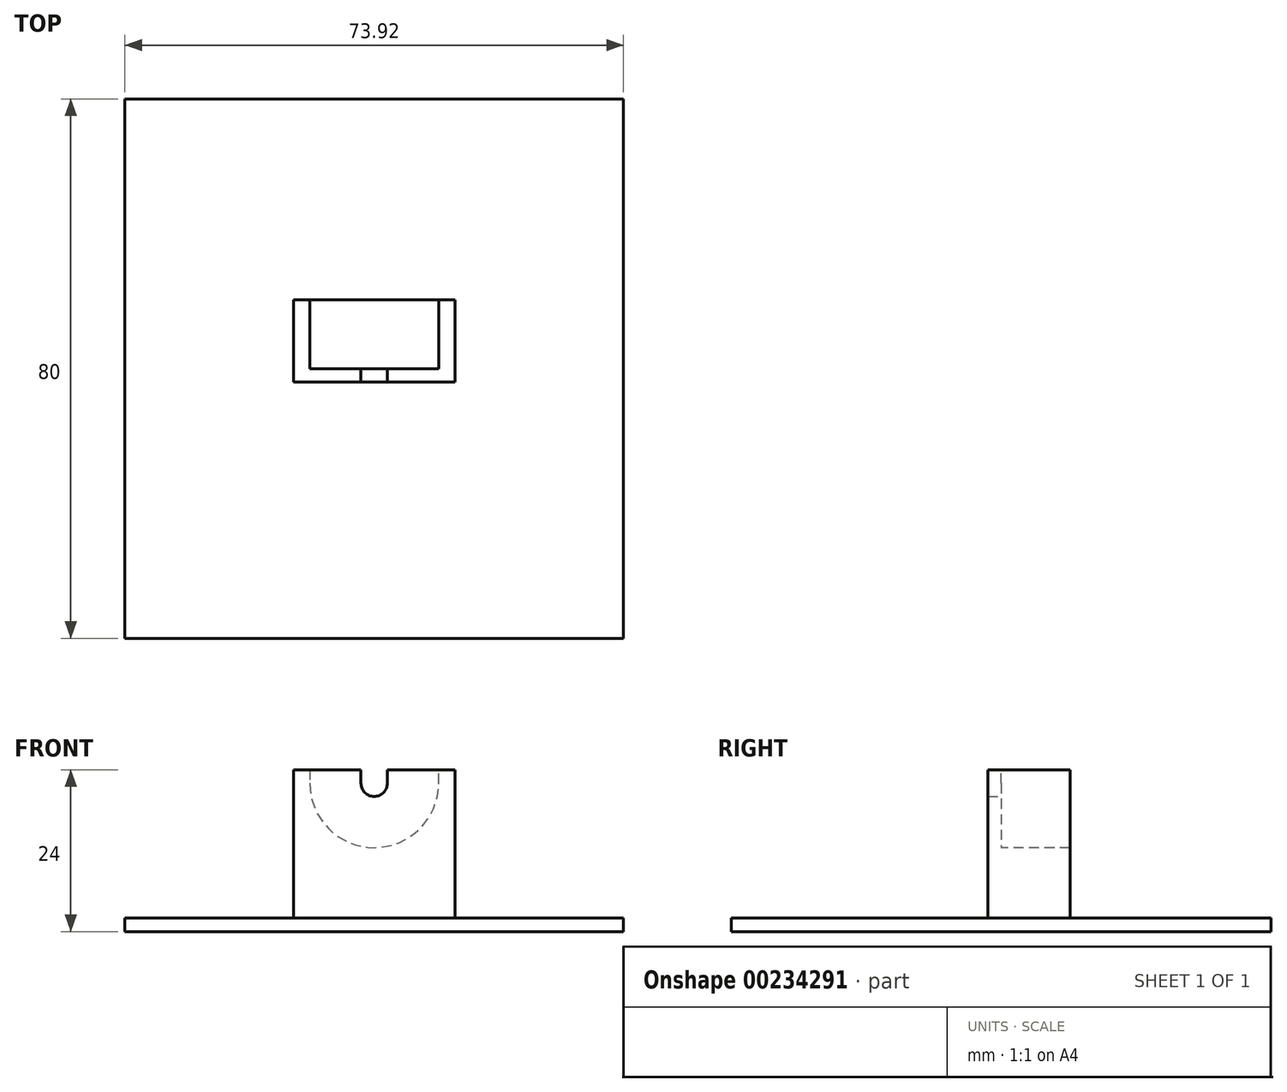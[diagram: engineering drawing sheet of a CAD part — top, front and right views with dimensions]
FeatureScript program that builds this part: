
annotation { "Feature Type Name" : "Feature", "Feature Type Description" : "" }
export const myFeature = defineFeature(function(context is Context, id is Id, definition is map)
    precondition{}
    {
        {
            var Q0;
            Q0=qCreatedBy(makeId("Front.planeOp"),FACE);
            var sketch = newSketch(context, id + "F0", { "sketchPlane" : qUnion([Q0])});
            skArc(sketch, "E0", {"start": v(-1.96, 0) * mm, "mid": v(0, -1.96) * mm, "end": v(1.96, 0) * mm});
            skLineSegment(sketch, "E1", {"start": v(1.96, 0) * mm, "end": v(11.96, 0) * mm});
            skLineSegment(sketch, "E2", {"start": v(-1.96, 0) * mm, "end": v(-11.96, 0) * mm});
            skLineSegment(sketch, "E3", {"start": v(-11.96, 0) * mm, "end": v(-11.96, -20) * mm});
            skLineSegment(sketch, "E4", {"start": v(11.96, 0) * mm, "end": v(11.96, -20) * mm});
            skLineSegment(sketch, "E5", {"start": v(-11.96, -20) * mm, "end": v(11.96, -20) * mm});
            skLineSegment(sketch, "E6", {"start": v(11.96, -20) * mm, "end": v(36.96, -20) * mm});
            skLineSegment(sketch, "E7", {"start": v(36.96, -20) * mm, "end": v(36.96, -22) * mm});
            skLineSegment(sketch, "E8", {"start": v(-11.96, -20) * mm, "end": v(-36.96, -20) * mm});
            skLineSegment(sketch, "E9", {"start": v(-36.96, -20) * mm, "end": v(-36.96, -22) * mm});
            skLineSegment(sketch, "E10", {"start": v(-36.96, -22) * mm, "end": v(36.96, -22) * mm});
            skLineSegment(sketch, "E11", {"start": v(-11.96, 0) * mm, "end": v(-11.96, 2) * mm});
            skLineSegment(sketch, "E12", {"start": v(-11.96, 2) * mm, "end": v(-1.96, 2) * mm});
            skLineSegment(sketch, "E13", {"start": v(-1.96, 2) * mm, "end": v(-1.96, 0) * mm});
            skLineSegment(sketch, "E14", {"start": v(11.96, 0) * mm, "end": v(11.96, 2) * mm});
            skLineSegment(sketch, "E15", {"start": v(1.96, 0) * mm, "end": v(1.96, 2) * mm});
            skLineSegment(sketch, "E16", {"start": v(1.96, 2) * mm, "end": v(11.96, 2) * mm});
            skSolve(sketch);
        }
        {
            var Q0;
            Q0=makeQuery(id+"F0.imprint","IMPRINT",FACE,{"disambiguationData":[TD([[makeQuery(id+"F0.imprint","IMPRINT",EDGE,{"derivedFrom":sQuery(id+"F0.wireOp",EDGE,"E1")}),1.0]])]});
            var Q1;
            Q1=makeQuery(id+"F0.imprint","IMPRINT",FACE,{"disambiguationData":[TD([[makeQuery(id+"F0.imprint","IMPRINT",EDGE,{"derivedFrom":sQuery(id+"F0.wireOp",EDGE,"E2")}),-1.0]])]});
            var Q2;
            Q2=makeQuery(id+"F0.imprint","IMPRINT",FACE,{"disambiguationData":[TD([[makeQuery(id+"F0.imprint","IMPRINT",EDGE,{"derivedFrom":sQuery(id+"F0.wireOp",EDGE,"E0")}),-1.0]])]});
            extrude(context, id + "F1", {"entities" : qUnion([Q0, Q1, Q2]), "depth" : 2 * mm});
        }
        {
            var Q0;
            Q0=qCreatedBy(makeId("Front.planeOp"),FACE);
            var sketch = newSketch(context, id + "F2", { "sketchPlane" : qUnion([Q0])});
            skArc(sketch, "E17", {"start": v(-9.55, 0) * mm, "mid": v(0, -9.55) * mm, "end": v(9.55, 0) * mm});
            skLineSegment(sketch, "E18", {"start": v(9.55, 0) * mm, "end": v(11.96, 0) * mm});
            skLineSegment(sketch, "E19", {"start": v(11.96, 0) * mm, "end": v(11.96, -20) * mm});
            skLineSegment(sketch, "E20", {"start": v(-9.55, 0) * mm, "end": v(-11.96, 0) * mm});
            skLineSegment(sketch, "E21", {"start": v(-11.96, 0) * mm, "end": v(-11.96, -20) * mm});
            skLineSegment(sketch, "E22", {"start": v(-11.96, -20) * mm, "end": v(11.96, -20) * mm});
            skLineSegment(sketch, "E23", {"start": v(11.96, 0) * mm, "end": v(11.96, 2) * mm});
            skLineSegment(sketch, "E24", {"start": v(9.55, 0) * mm, "end": v(9.55, 2) * mm});
            skLineSegment(sketch, "E25", {"start": v(9.55, 2) * mm, "end": v(11.96, 2) * mm});
            skLineSegment(sketch, "E26", {"start": v(-11.96, 0) * mm, "end": v(-11.96, 2) * mm});
            skLineSegment(sketch, "E27", {"start": v(-11.96, 2) * mm, "end": v(-9.55, 2) * mm});
            skLineSegment(sketch, "E28", {"start": v(-9.55, 2) * mm, "end": v(-9.55, 0) * mm});
            skSolve(sketch);
        }
        {
            var Q0;
            Q0 = qSketchRegion(id + "F2", true);
            extrude(context, id + "F3", {"entities" : qUnion([Q0]), "operationType" : NewBodyOperationType.ADD, "oppositeDirection" : true, "depth" : 10.2 * mm});
        }
        {
            var Q0;
            Q0=makeQuery(id+"F0.imprint","IMPRINT",FACE,{"disambiguationData":[TD([[makeQuery(id+"F0.imprint","IMPRINT",EDGE,{"derivedFrom":sQuery(id+"F0.wireOp",EDGE,"E5")}),-1.0]])]});
            extrude(context, id + "F4", {"entities" : qUnion([Q0]), "operationType" : NewBodyOperationType.ADD, "endBound" : BoundingType.SYMMETRIC, "depth" : 80 * mm});
        }
    });
